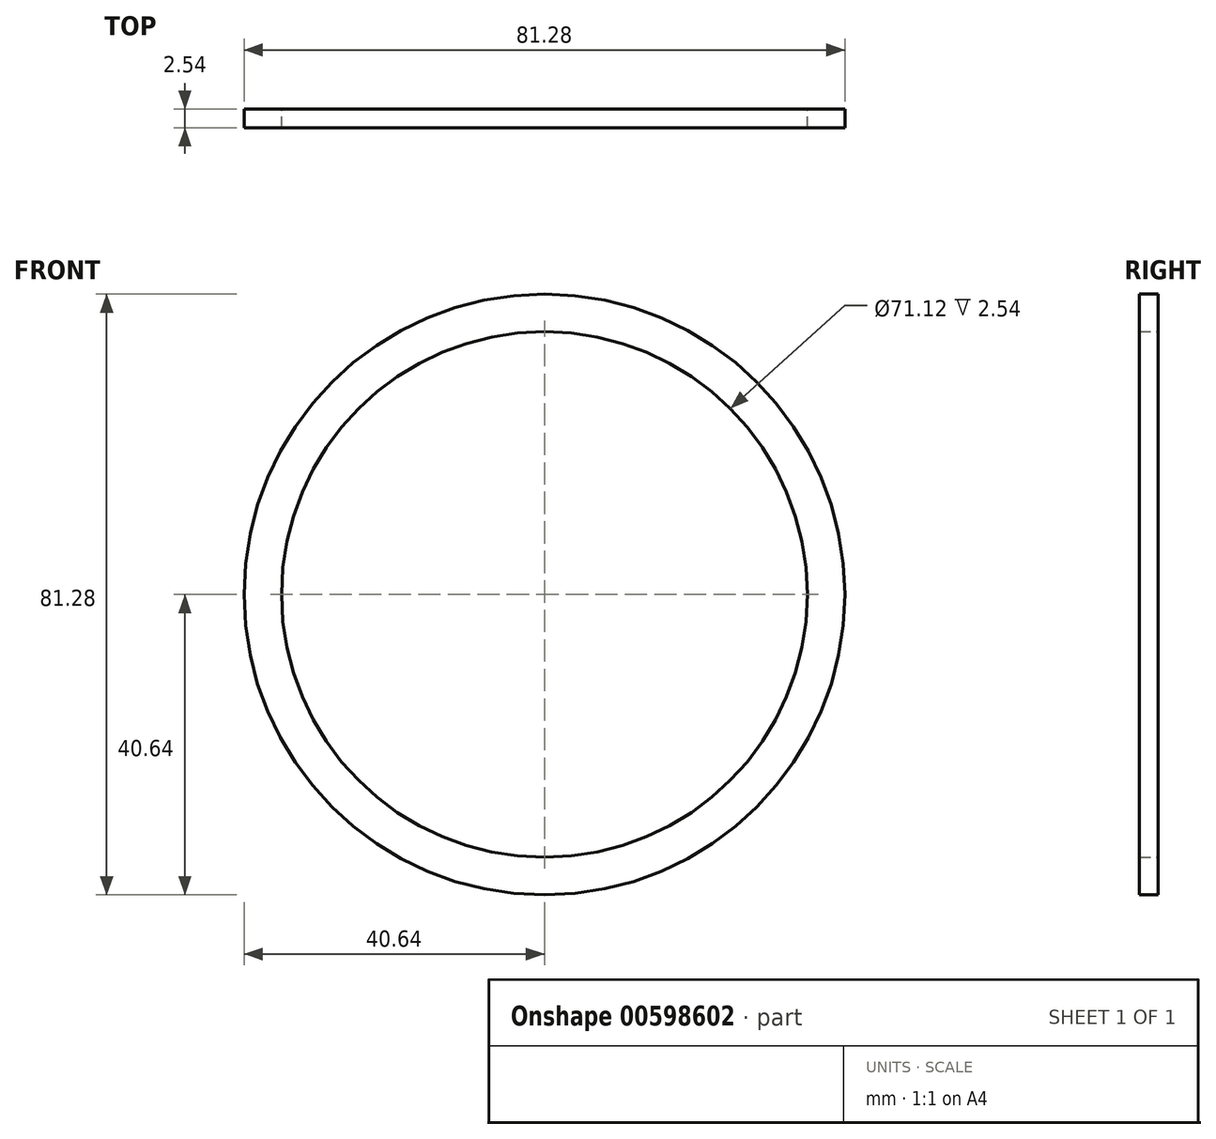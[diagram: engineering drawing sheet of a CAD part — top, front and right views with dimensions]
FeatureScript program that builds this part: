
annotation { "Feature Type Name" : "Feature", "Feature Type Description" : "" }
export const myFeature = defineFeature(function(context is Context, id is Id, definition is map)
    precondition{}
    {
        {
            var Q0;
            Q0=qCreatedBy(makeId("Front.planeOp"),FACE);
            var sketch = newSketch(context, id + "F0", { "sketchPlane" : qUnion([Q0])});
            skCircle(sketch, "E0", {"center": v(0, 0) * mm, "radius": 35.56 * mm});
            skCircle(sketch, "E1", {"center": v(0, 0) * mm, "radius": 40.64 * mm});
            skSolve(sketch);
        }
        {
            var Q0;
            Q0 = qSketchRegion(id + "F0", true);
            extrude(context, id + "F1", {"entities" : qUnion([Q0]), "depth" : 2.54 * mm, "offsetDistance" : 25.4 * mm});
        }
    });
